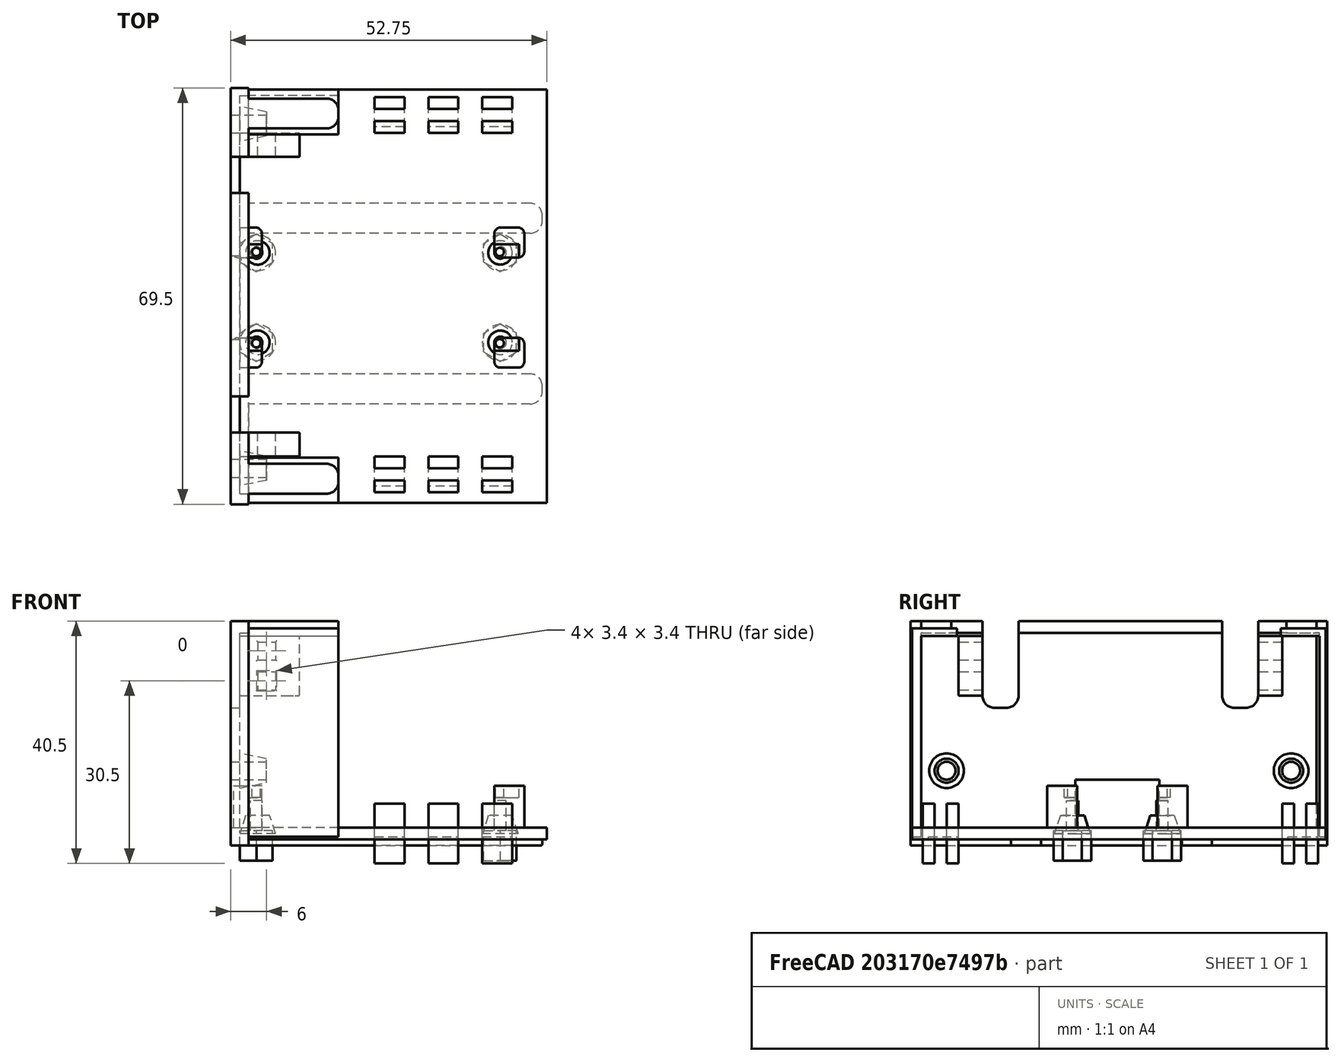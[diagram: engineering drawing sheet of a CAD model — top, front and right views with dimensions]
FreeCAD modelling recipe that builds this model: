
FCSTD DOCUMENT  (FreeCAD 0.19R24291 (Git))
Label: Arduino_Nano_33_BLE_tray_alt
License: All rights reserved
LicenseURL: http://en.wikipedia.org/wiki/All_rights_reserved
objects: Part::Box×67, Part::MultiFuse×33, Part::Fillet×18, Part::Cut×12, Part::Cylinder×10, Part::Cone×6, Part::MultiCommon×4
note: 150 computed .brp shape members not serialized (recipe doc carries the construction recipe); baked Part::Feature solids carry a one-line shape summary decoded from their .brp

FEATURE [Part::Box] Box  label="Board"
  AttacherType = Attacher::AttachEngine3D
  Height = 10
  Length = 45.16
  Width = 17.76
FEATURE [Part::Cylinder] Cylinder
  Angle = 360
  AttacherType = Attacher::AttachEngine3D
  Height = 10
  Placement = pos=(1.26,1.26,0) rot=(0,0,1;0rad)
  Radius = 0.7
FEATURE [Part::Cylinder] Cylinder001
  Angle = 360
  AttacherType = Attacher::AttachEngine3D
  Height = 10
  Placement = pos=(41.9,1.26,0) rot=(0,0,1;0rad)
  Radius = 0.7
FEATURE [Part::Cylinder] Cylinder002
  Angle = 360
  AttacherType = Attacher::AttachEngine3D
  Height = 10
  Placement = pos=(1.26,16.5,0) rot=(0,0,1;0rad)
  Radius = 0.7
FEATURE [Part::Cylinder] Cylinder003
  Angle = 360
  AttacherType = Attacher::AttachEngine3D
  Height = 10
  Placement = pos=(41.9,16.5,0) rot=(0,0,1;0rad)
  Radius = 0.7
FEATURE [Part::MultiFuse] Fusion  label="Holes"
  Shapes = -> [Cylinder,Cylinder001,Cylinder002,Cylinder003]
FEATURE [Part::Cut] Cut  label="Arduino_board_shape"
  Base = -> Box
  Placement = pos=(0,25.62,3) rot=(0,0,1;0rad)
  Tool = -> Fusion
FEATURE [Part::Box] Box001  label="Cube"
  AttacherType = Attacher::AttachEngine3D
  Height = 37.5
  Length = 3
  Placement = pos=(-3,0,0) rot=(0,0,1;0rad)
  Width = 69.5
FEATURE [Part::Box] Box002  label="Cube001"
  AttacherType = Attacher::AttachEngine3D
  Height = 2
  Length = 50
  Placement = pos=(-0.25,0.25,1) rot=(0,0,1;0rad)
  Width = 69
FEATURE [Part::Box] Box003  label="Cube002"
  AttacherType = Attacher::AttachEngine3D
  Height = 34.75
  Length = 15
  Placement = pos=(0,0,2) rot=(0,0,1;0rad)
  Width = 7.5
FEATURE [Part::Box] Box004  label="Cube003"
  AttacherType = Attacher::AttachEngine3D
  Height = 34.75
  Length = 15
  Placement = pos=(0,61.5,2) rot=(0,0,1;0rad)
  Width = 7.5
FEATURE [Part::Box] Box005  label="Cube004"
  AttacherType = Attacher::AttachEngine3D
  Height = 34
  Length = 15
  Placement = pos=(0,1.5,1) rot=(0,0,1;0rad)
  Width = 7.5
FEATURE [Part::Box] Box006  label="Cube005"
  AttacherType = Attacher::AttachEngine3D
  Height = 34
  Length = 15
  Placement = pos=(0,60,1) rot=(0,0,1;0rad)
  Width = 7.5
FEATURE [Part::MultiFuse] Fusion001
  Shapes = -> [Box006,Box005]
FEATURE [Part::MultiFuse] Fusion002
  Placement = pos=(0,0,-0.5) rot=(0,0,1;0rad)
  Shapes = -> [Box004,Box003]
FEATURE [Part::Cut] Cut001
  Base = -> Fusion002
  Placement = pos=(0,0.25,0) rot=(0,0,1;0rad)
  Tool = -> Fusion001
FEATURE [Part::Box] Box007  label="Cube006"
  AttacherType = Attacher::AttachEngine3D
  Height = 32.5
  Length = 3.5
  Placement = pos=(-1.5,1.75,3) rot=(0,0,1;0rad)
  Width = 66.5
FEATURE [Part::Cut] Cut002
  Base = -> Box001
  Tool = -> Box007
FEATURE [Part::Cylinder] Cylinder004
  Angle = 360
  AttacherType = Attacher::AttachEngine3D
  Height = 10
  Placement = pos=(-5,6,32.5) rot=(0,1,0;1.5708rad)
  Radius = 1.5
FEATURE [Part::Cylinder] Cylinder005
  Angle = 360
  AttacherType = Attacher::AttachEngine3D
  Height = 10
  Placement = pos=(-5,63.5,32.5) rot=(0,1,0;1.5708rad)
  Radius = 1.5
FEATURE [Part::MultiFuse] Fusion003
  Placement = pos=(0,0,-20) rot=(0,0,1;0rad)
  Shapes = -> [Cylinder004,Cylinder005]
FEATURE [Part::Box] Box008  label="Cube007"
  AttacherType = Attacher::AttachEngine3D
  Height = 8
  Length = 10
  Placement = pos=(-5,27.5,3) rot=(0,0,1;0rad)
  Width = 14
FEATURE [Part::Cone] Cone
  Angle = 360
  AttacherType = Attacher::AttachEngine3D
  Height = 5
  Placement = pos=(-1,6,32.5) rot=(0,1,0;1.5708rad)
  Radius1 = 3
  Radius2 = 2
FEATURE [Part::Cone] Cone001
  Angle = 360
  AttacherType = Attacher::AttachEngine3D
  Height = 5
  Placement = pos=(-1,63.5,32.5) rot=(0,1,0;1.5708rad)
  Radius1 = 3
  Radius2 = 2
FEATURE [Part::MultiFuse] Fusion004
  Placement = pos=(-1,0,-20) rot=(0,0,1;0rad)
  Shapes = -> [Cone,Cone001]
  expr: .Placement.Base.z = -20
FEATURE [Part::MultiFuse] Fusion005
  Shapes = -> [Cut002,Fusion004]
FEATURE [Part::Cut] Cut003
  Base = -> Fusion005
  Tool = -> Fusion003
FEATURE [Part::Cut] Cut004
  Base = -> Cut003
  Tool = -> Box008
FEATURE [Part::Cone] Cone002
  Angle = 360
  AttacherType = Attacher::AttachEngine3D
  Height = 3
  Placement = pos=(42,27,2) rot=(0,0,1;0rad)
  Radius1 = 3
  Radius2 = 2
FEATURE [Part::Box] Box014  label="Cube014"
  AttacherType = Attacher::AttachEngine3D
  Height = 5
  Length = 5.45
  Placement = pos=(3.25,0,0) rot=(0,0,1;0rad)
  Width = 10
FEATURE [Part::Box] Box015  label="Cube015"
  AttacherType = Attacher::AttachEngine3D
  Height = 5
  Length = 5.45
  Placement = pos=(11.5,4,0) rot=(0,0,1;2.0944rad)
  Width = 10
FEATURE [Part::Box] Box016  label="Cube016"
  AttacherType = Attacher::AttachEngine3D
  Height = 5
  Length = 10
  Placement = pos=(0.55,4,0) rot=(0,0,-1;0.523599rad)
  Width = 5.45
FEATURE [Part::Cylinder] Cylinder006
  Angle = 360
  AttacherType = Attacher::AttachEngine3D
  Height = 10
  Placement = pos=(4,4,-1) rot=(0,0,1;0rad)
  Radius = 1
FEATURE [Part::MultiCommon] Common  label="M.25 nut"
  Placement = pos=(-2,0,-1) rot=(0,0,1;0rad)
  Shapes = -> [Box014,Box016,Box015]
FEATURE [Part::MultiFuse] Fusion008  label="screw_hole"
  Placement = pos=(-2.7,23,0) rot=(0,0,1;0rad)
  Shapes = -> [Cylinder006,Common]
FEATURE [Part::Cone] Cone003
  Angle = 360
  AttacherType = Attacher::AttachEngine3D
  Height = 3
  Placement = pos=(42,42,2) rot=(0,0,1;0rad)
  Radius1 = 3
  Radius2 = 2
FEATURE [Part::Cone] Cone004
  Angle = 360
  AttacherType = Attacher::AttachEngine3D
  Height = 3
  Placement = pos=(1.5,42,2) rot=(0,0,1;0rad)
  Radius1 = 3
  Radius2 = 2
FEATURE [Part::Cone] Cone005
  Angle = 360
  AttacherType = Attacher::AttachEngine3D
  Height = 3
  Placement = pos=(1.5,27,2) rot=(0,0,1;0rad)
  Radius1 = 3
  Radius2 = 2
FEATURE [Part::Box] Box017  label="Cube017"
  AttacherType = Attacher::AttachEngine3D
  Height = 5
  Length = 5.45
  Placement = pos=(3.25,0,0) rot=(0,0,1;0rad)
  Width = 10
FEATURE [Part::Box] Box018  label="Cube018"
  AttacherType = Attacher::AttachEngine3D
  Height = 5
  Length = 5.45
  Placement = pos=(11.5,4,0) rot=(0,0,1;2.0944rad)
  Width = 10
FEATURE [Part::Cylinder] Cylinder007
  Angle = 360
  AttacherType = Attacher::AttachEngine3D
  Height = 10
  Placement = pos=(4,4,-1) rot=(0,0,1;0rad)
  Radius = 1
FEATURE [Part::Box] Box019  label="Cube019"
  AttacherType = Attacher::AttachEngine3D
  Height = 5
  Length = 10
  Placement = pos=(0.55,4,0) rot=(0,0,-1;0.523599rad)
  Width = 5.45
FEATURE [Part::MultiCommon] Common001  label="M.25 nut001"
  Placement = pos=(-2,0,-1) rot=(0,0,1;0rad)
  Shapes = -> [Box017,Box019,Box018]
FEATURE [Part::MultiFuse] Fusion009  label="screw_hole001"
  Placement = pos=(-2.7,38,0) rot=(0,0,1;0rad)
  Shapes = -> [Cylinder007,Common001]
FEATURE [Part::Box] Box020  label="Cube020"
  AttacherType = Attacher::AttachEngine3D
  Height = 5
  Length = 5.45
  Placement = pos=(3.25,0,0) rot=(0,0,1;0rad)
  Width = 10
FEATURE [Part::Box] Box021  label="Cube021"
  AttacherType = Attacher::AttachEngine3D
  Height = 5
  Length = 5.45
  Placement = pos=(11.5,4,0) rot=(0,0,1;2.0944rad)
  Width = 10
FEATURE [Part::Cylinder] Cylinder008
  Angle = 360
  AttacherType = Attacher::AttachEngine3D
  Height = 10
  Placement = pos=(4,4,-1) rot=(0,0,1;0rad)
  Radius = 1
FEATURE [Part::Box] Box022  label="Cube022"
  AttacherType = Attacher::AttachEngine3D
  Height = 5
  Length = 10
  Placement = pos=(0.55,4,0) rot=(0,0,-1;0.523599rad)
  Width = 5.45
FEATURE [Part::MultiCommon] Common002  label="M.25 nut002"
  Placement = pos=(-2,0,-1) rot=(0,0,1;0rad)
  Shapes = -> [Box020,Box022,Box021]
FEATURE [Part::MultiFuse] Fusion010  label="screw_hole002"
  Placement = pos=(38,23,0) rot=(0,0,1;0rad)
  Shapes = -> [Cylinder008,Common002]
FEATURE [Part::Box] Box023  label="Cube023"
  AttacherType = Attacher::AttachEngine3D
  Height = 5
  Length = 5.45
  Placement = pos=(3.25,0,0) rot=(0,0,1;0rad)
  Width = 10
FEATURE [Part::Box] Box024  label="Cube024"
  AttacherType = Attacher::AttachEngine3D
  Height = 5
  Length = 5.45
  Placement = pos=(11.5,4,0) rot=(0,0,1;2.0944rad)
  Width = 10
FEATURE [Part::Cylinder] Cylinder009
  Angle = 360
  AttacherType = Attacher::AttachEngine3D
  Height = 10
  Placement = pos=(4,4,-1) rot=(0,0,1;0rad)
  Radius = 1
FEATURE [Part::Box] Box025  label="Cube025"
  AttacherType = Attacher::AttachEngine3D
  Height = 5
  Length = 10
  Placement = pos=(0.55,4,0) rot=(0,0,-1;0.523599rad)
  Width = 5.45
FEATURE [Part::MultiCommon] Common003  label="M.25 nut003"
  Placement = pos=(-2,0,-1) rot=(0,0,1;0rad)
  Shapes = -> [Box023,Box025,Box024]
FEATURE [Part::MultiFuse] Fusion011  label="screw_hole003"
  Placement = pos=(38,38,0) rot=(0,0,1;0rad)
  Shapes = -> [Cylinder009,Common003]
FEATURE [Part::MultiFuse] Fusion012  label="Screw holes cut"
  Placement = pos=(0,0,-1.5) rot=(0,0,1;0rad)
  Shapes = -> [Fusion008,Fusion009,Fusion010,Fusion011]
FEATURE [Part::MultiFuse] Fusion014
  Shapes = -> [Cut004,Box002]
FEATURE [Part::MultiFuse] Fusion015
  Shapes = -> [Cut001]
FEATURE [Part::Box] Box026  label="Cube026"
  AttacherType = Attacher::AttachEngine3D
  Height = 15
  Length = 10
  Placement = pos=(0,0,16) rot=(0,0,1;0rad)
  Width = 6
FEATURE [Part::Fillet] Fillet012
  Base = -> Box026
  Edges = 2 edges r=2: [Edge9,Edge11]
  Placement = pos=(-4,12,7) rot=(0,0,1;0rad)
FEATURE [Part::Box] Box027  label="Cube027"
  AttacherType = Attacher::AttachEngine3D
  Height = 15
  Length = 10
  Placement = pos=(0,0,16) rot=(0,0,1;0rad)
  Width = 6
FEATURE [Part::Fillet] Fillet013
  Base = -> Box027
  Edges = 2 edges r=2: [Edge9,Edge11]
  Placement = pos=(-4,52,7) rot=(0,0,1;0rad)
FEATURE [Part::MultiFuse] Fusion016  label="Cables sockets"
  Shapes = -> [Fillet012,Fillet013]
FEATURE [Part::Cut] Cut006  label="Arduino_Nano_33_BLE_tray"
  Base = -> Fusion015
  Tool = -> Fusion016
FEATURE [Part::Box] Box028  label="Cube028"
  AttacherType = Attacher::AttachEngine3D
  Height = 2
  Length = 15
  Placement = pos=(0,-15.5,0) rot=(0,0,1;0rad)
  Width = 5
FEATURE [Part::Fillet] Fillet
  Base = -> Box028
  Edges = 2 edges r=2: [Edge5,Edge7]
  Placement = pos=(0,17,0) rot=(0,0,1;0rad)
FEATURE [Part::Box] Box029  label="Cube029"
  AttacherType = Attacher::AttachEngine3D
  Height = 2
  Length = 49
  Width = 5
FEATURE [Part::Fillet] Fillet014
  Base = -> Box029
  Edges = 2 edges r=2: [Edge5,Edge7]
  Placement = pos=(0,45,0) rot=(0,0,1;0rad)
FEATURE [Part::Fillet] Fillet015
  Base = -> Fillet
  Edges = 2 edges r=0.25: [Edge14,Edge16]
  Placement = pos=(0,0.25,35.5) rot=(0,0,1;0rad)
FEATURE [Part::Fillet] Fillet016
  Base = -> Fillet014
  Edges = 2 edges r=0.25: [Edge14,Edge16]
  Placement = pos=(0,0.25,0) rot=(0,0,1;0rad)
FEATURE [Part::Box] Box030  label="Cube030"
  AttacherType = Attacher::AttachEngine3D
  Height = 2
  Length = 49
  Width = 5
FEATURE [Part::Fillet] Fillet017
  Base = -> Box030
  Edges = 2 edges r=2: [Edge5,Edge7]
  Placement = pos=(0,17,0) rot=(0,0,1;0rad)
FEATURE [Part::Fillet] Fillet018
  Base = -> Fillet017
  Edges = 2 edges r=0.25: [Edge14,Edge16]
  Placement = pos=(0,-0.25,0) rot=(0,0,1;0rad)
FEATURE [Part::Box] Box031  label="Cube031"
  AttacherType = Attacher::AttachEngine3D
  Height = 2
  Length = 15
  Placement = pos=(0,-15.25,0) rot=(0,0,1;0rad)
  Width = 5
FEATURE [Part::Fillet] Fillet019
  Base = -> Box031
  Edges = 2 edges r=2: [Edge5,Edge7]
  Placement = pos=(0,17,0) rot=(0,0,1;0rad)
FEATURE [Part::Fillet] Fillet020
  Base = -> Fillet019
  Edges = 2 edges r=0.25: [Edge14,Edge16]
  Placement = pos=(0,61,35.5) rot=(0,0,1;0rad)
FEATURE [Part::MultiFuse] Fusion017  label="rails"
  Shapes = -> [Fillet015,Fillet016,Fillet018,Fillet020]
FEATURE [Part::MultiFuse] Fusion018  label="Arduino tray rough"
  Shapes = -> [Cut006,Fusion017]
FEATURE [Part::Box] Box032  label="Cube032"
  AttacherType = Attacher::AttachEngine3D
  Height = 10
  Length = 10
  Placement = pos=(0,8,26) rot=(0,0,1;0rad)
  Width = 4
FEATURE [Part::Box] Box033  label="Cube033"
  AttacherType = Attacher::AttachEngine3D
  Height = 3
  Length = 3
  Placement = pos=(3,5,27) rot=(0,0,1;0rad)
  Width = 10
FEATURE [Part::Box] Box034  label="Cube034"
  AttacherType = Attacher::AttachEngine3D
  Height = 3
  Length = 3
  Placement = pos=(3,5,32) rot=(0,0,1;0rad)
  Width = 10
FEATURE [Part::MultiFuse] Fusion019
  Shapes = -> [Box033,Box034]
FEATURE [Part::Cut] Cut007
  Base = -> Box032
  Tool = -> Fusion019
FEATURE [Part::Fillet] Fillet022  label="zip ties holder"
  Base = -> Cut007
  Edges = 22 edges r=0.2: [Edge5,Edge6,Edge7,Edge8,Edge9,Edge10,Edge11,Edge12,Edge13,Edge14,Edge15,Edge16,Edge19,Edge20,Edge21,Edge22,Edge23,Edge24,Edge25,Edge26,Edge27,Edge28]
  Placement = pos=(-1,0,-1) rot=(0,0,1;0rad)
FEATURE [Part::Box] Box035  label="Cube035"
  AttacherType = Attacher::AttachEngine3D
  Height = 10
  Length = 10
  Placement = pos=(0,10,26) rot=(0,0,1;0rad)
  Width = 4
FEATURE [Part::Box] Box036  label="Cube036"
  AttacherType = Attacher::AttachEngine3D
  Height = 3
  Length = 3
  Placement = pos=(3,10,27) rot=(0,0,1;0rad)
  Width = 10
FEATURE [Part::Box] Box037  label="Cube037"
  AttacherType = Attacher::AttachEngine3D
  Height = 3
  Length = 3
  Placement = pos=(3,10,32) rot=(0,0,1;0rad)
  Width = 10
FEATURE [Part::MultiFuse] Fusion020
  Shapes = -> [Box036,Box037]
FEATURE [Part::Cut] Cut008
  Base = -> Box035
  Tool = -> Fusion020
FEATURE [Part::Fillet] Fillet023  label="zip ties holder001"
  Base = -> Cut008
  Edges = 22 edges r=0.2: [Edge5,Edge6,Edge7,Edge8,Edge9,Edge10,Edge11,Edge12,Edge13,Edge14,Edge15,Edge16,Edge19,Edge20,Edge21,Edge22,Edge23,Edge24,Edge25,Edge26,Edge27,Edge28]
  Placement = pos=(-1,48,-1) rot=(0,0,1;0rad)
FEATURE [Part::MultiFuse] Fusion021  label="zip ties holders"
  Placement = pos=(-0.5,0,0) rot=(0,0,1;0rad)
  Shapes = -> [Fillet022,Fillet023]
FEATURE [Part::Box] Box038  label="Cube038"
  AttacherType = Attacher::AttachEngine3D
  Height = 10
  Length = 5
  Placement = pos=(21,2,-3) rot=(0,0,1;0rad)
  Width = 2
FEATURE [Part::Box] Box039  label="Cube039"
  AttacherType = Attacher::AttachEngine3D
  Height = 10
  Length = 5
  Placement = pos=(30,2,-3) rot=(0,0,1;0rad)
  Width = 2
FEATURE [Part::Box] Box040  label="Cube040"
  AttacherType = Attacher::AttachEngine3D
  Height = 10
  Length = 5
  Placement = pos=(39,2,-3) rot=(0,0,1;0rad)
  Width = 2
FEATURE [Part::MultiFuse] Fusion022  label="zip ties holes board r"
  Shapes = -> [Box038,Box039,Box040]
FEATURE [Part::Box] Box041  label="Cube041"
  AttacherType = Attacher::AttachEngine3D
  Height = 10
  Length = 5
  Placement = pos=(21,2,-3) rot=(0,0,1;0rad)
  Width = 2
FEATURE [Part::Box] Box042  label="Cube042"
  AttacherType = Attacher::AttachEngine3D
  Height = 10
  Length = 5
  Placement = pos=(30,2,-3) rot=(0,0,1;0rad)
  Width = 2
FEATURE [Part::Box] Box043  label="Cube043"
  AttacherType = Attacher::AttachEngine3D
  Height = 10
  Length = 5
  Placement = pos=(39,2,-3) rot=(0,0,1;0rad)
  Width = 2
FEATURE [Part::MultiFuse] Fusion023  label="zip ties holes board l"
  Placement = pos=(0,64,0) rot=(0,0,1;0rad)
  Shapes = -> [Box041,Box042,Box043]
FEATURE [Part::Box] Box044  label="Cube044"
  AttacherType = Attacher::AttachEngine3D
  Height = 10
  Length = 5
  Placement = pos=(21,2,-3) rot=(0,0,1;0rad)
  Width = 2
FEATURE [Part::Box] Box045  label="Cube045"
  AttacherType = Attacher::AttachEngine3D
  Height = 10
  Length = 5
  Placement = pos=(30,2,-3) rot=(0,0,1;0rad)
  Width = 2
FEATURE [Part::Box] Box046  label="Cube046"
  AttacherType = Attacher::AttachEngine3D
  Height = 10
  Length = 5
  Placement = pos=(39,2,-3) rot=(0,0,1;0rad)
  Width = 2
FEATURE [Part::MultiFuse] Fusion024  label="zip ties holes board r001"
  Placement = pos=(0,4,0) rot=(0,0,1;0rad)
  Shapes = -> [Box044,Box045,Box046]
FEATURE [Part::Box] Box047  label="Cube047"
  AttacherType = Attacher::AttachEngine3D
  Height = 10
  Length = 5
  Placement = pos=(21,2,-3) rot=(0,0,1;0rad)
  Width = 2
FEATURE [Part::Box] Box048  label="Cube048"
  AttacherType = Attacher::AttachEngine3D
  Height = 10
  Length = 5
  Placement = pos=(30,2,-3) rot=(0,0,1;0rad)
  Width = 2
FEATURE [Part::Box] Box049  label="Cube049"
  AttacherType = Attacher::AttachEngine3D
  Height = 10
  Length = 5
  Placement = pos=(39,2,-3) rot=(0,0,1;0rad)
  Width = 2
FEATURE [Part::MultiFuse] Fusion025  label="zip ties holes board l001"
  Placement = pos=(0,60,0) rot=(0,0,1;0rad)
  Shapes = -> [Box047,Box048,Box049]
FEATURE [Part::MultiFuse] Fusion026  label="zip ties holes"
  Shapes = -> [Fusion022,Fusion023,Fusion024,Fusion025]
FEATURE [Part::MultiFuse] Fusion027  label="Arduino_tray"
  Shapes = -> [Fusion021]
FEATURE [Part::Box] Box050  label="Cube050"
  AttacherType = Attacher::AttachEngine3D
  Height = 1.5
  Length = 5
  Placement = pos=(21,3,0) rot=(0,0,1;0rad)
  Width = 5
FEATURE [Part::Box] Box051  label="Cube051"
  AttacherType = Attacher::AttachEngine3D
  Height = 1.5
  Length = 5
  Placement = pos=(30,3,0) rot=(0,0,1;0rad)
  Width = 5
FEATURE [Part::Box] Box052  label="Cube052"
  AttacherType = Attacher::AttachEngine3D
  Height = 1.5
  Length = 5
  Placement = pos=(39,3,0) rot=(0,0,1;0rad)
  Width = 5
FEATURE [Part::Box] Box053  label="Cube053"
  AttacherType = Attacher::AttachEngine3D
  Height = 1.5
  Length = 5
  Placement = pos=(39,63,0) rot=(0,0,1;0rad)
  Width = 5
FEATURE [Part::Box] Box054  label="Cube054"
  AttacherType = Attacher::AttachEngine3D
  Height = 1.5
  Length = 5
  Placement = pos=(30,63,0) rot=(0,0,1;0rad)
  Width = 5
FEATURE [Part::Box] Box055  label="Cube055"
  AttacherType = Attacher::AttachEngine3D
  Height = 1.5
  Length = 5
  Placement = pos=(21,63,0) rot=(0,0,1;0rad)
  Width = 5
FEATURE [Part::MultiFuse] Fusion028
  Shapes = -> [Box050,Box051,Box052,Box053,Box054,Box055]
FEATURE [Part::Cut] Cut010
  Base = -> Fusion027
  Tool = -> Fusion028
FEATURE [Part::Box] Box056  label="Cube056"
  AttacherType = Attacher::AttachEngine3D
  Height = 7
  Length = 5
  Placement = pos=(-2.8,22.8,-2) rot=(0,0,1;0rad)
  Width = 5
FEATURE [Part::Box] Box057  label="Cube057"
  AttacherType = Attacher::AttachEngine3D
  Height = 7
  Length = 5
  Placement = pos=(-2.8,41.2,-2) rot=(0,0,1;0rad)
  Width = 5
FEATURE [Part::Box] Box058  label="Cube058"
  AttacherType = Attacher::AttachEngine3D
  Height = 7
  Length = 5
  Placement = pos=(41,41.2,-2) rot=(0,0,1;0rad)
  Width = 5
FEATURE [Part::Box] Box059  label="Cube059"
  AttacherType = Attacher::AttachEngine3D
  Height = 7
  Length = 5
  Placement = pos=(41,22.8,-2) rot=(0,0,1;0rad)
  Width = 5
FEATURE [Part::Fillet] Fillet024
  Base = -> Box056
  Edges = 4 edges r=1: [Edge1,Edge3,Edge5,Edge7]
FEATURE [Part::Fillet] Fillet025
  Base = -> Box057
  Edges = 4 edges r=1: [Edge1,Edge3,Edge5,Edge7]
FEATURE [Part::Fillet] Fillet026
  Base = -> Box058
  Edges = 4 edges r=1: [Edge1,Edge3,Edge5,Edge7]
FEATURE [Part::Fillet] Fillet027
  Base = -> Box059
  Edges = 4 edges r=1: [Edge1,Edge3,Edge5,Edge7]
FEATURE [Part::MultiFuse] Fusion029
  Shapes = -> [Fillet024,Fillet025,Fillet026,Fillet027]
FEATURE [Part::Cut] Cut011
  Base = -> Fusion029
  Placement = pos=(0,0,5) rot=(0,0,1;0rad)
  Tool = -> Cut
FEATURE [Part::Box] Box060  label="Cube060"
  AttacherType = Attacher::AttachEngine3D
  Height = 34.75
  Length = 15
  Placement = pos=(0,0,2) rot=(0,0,1;0rad)
  Width = 7.5
FEATURE [Part::Box] Box061  label="Cube061"
  AttacherType = Attacher::AttachEngine3D
  Height = 34.75
  Length = 15
  Placement = pos=(0,61.5,2) rot=(0,0,1;0rad)
  Width = 7.5
FEATURE [Part::Box] Box062  label="Cube062"
  AttacherType = Attacher::AttachEngine3D
  Height = 34
  Length = 15
  Placement = pos=(0,1.5,1) rot=(0,0,1;0rad)
  Width = 7.5
FEATURE [Part::Box] Box063  label="Cube063"
  AttacherType = Attacher::AttachEngine3D
  Height = 34
  Length = 15
  Placement = pos=(0,60.5,1) rot=(0,0,1;0rad)
  Width = 7.5
FEATURE [Part::MultiFuse] Fusion030
  Shapes = -> [Box063,Box062]
FEATURE [Part::MultiFuse] Fusion031
  Placement = pos=(0,0,-0.5) rot=(0,0,1;0rad)
  Shapes = -> [Box061,Box060]
FEATURE [Part::Cut] Cut012
  Base = -> Fusion031
  Placement = pos=(0,0.25,0) rot=(0,0,1;0rad)
  Tool = -> Fusion030
FEATURE [Part::Box] Box064  label="Cube064"
  AttacherType = Attacher::AttachEngine3D
  Height = 15
  Length = 10
  Placement = pos=(0,0,16) rot=(0,0,1;0rad)
  Width = 6
FEATURE [Part::Fillet] Fillet028
  Base = -> Box064
  Edges = 2 edges r=2: [Edge9,Edge11]
  Placement = pos=(-4,12,7) rot=(0,0,1;0rad)
FEATURE [Part::Box] Box065  label="Cube065"
  AttacherType = Attacher::AttachEngine3D
  Height = 15
  Length = 10
  Placement = pos=(0,0,16) rot=(0,0,1;0rad)
  Width = 6
FEATURE [Part::Fillet] Fillet029
  Base = -> Box065
  Edges = 2 edges r=2: [Edge9,Edge11]
  Placement = pos=(-4,52,7) rot=(0,0,1;0rad)
FEATURE [Part::MultiFuse] Fusion032  label="Cables sockets001"
  Shapes = -> [Fillet028,Fillet029]
FEATURE [Part::MultiFuse] Fusion033
  Shapes = -> [Fusion014,Fusion018,Cut010,Cut011]
FEATURE [Part::Box] Box066  label="Cube066"
  AttacherType = Attacher::AttachEngine3D
  Height = 1.5
  Length = 5
  Placement = pos=(21,3,0) rot=(0,0,1;0rad)
  Width = 5
FEATURE [Part::Box] Box067  label="Cube067"
  AttacherType = Attacher::AttachEngine3D
  Height = 1.5
  Length = 5
  Placement = pos=(30,3,0) rot=(0,0,1;0rad)
  Width = 5
FEATURE [Part::Box] Box068  label="Cube068"
  AttacherType = Attacher::AttachEngine3D
  Height = 1.5
  Length = 5
  Placement = pos=(39,3,0) rot=(0,0,1;0rad)
  Width = 5
FEATURE [Part::Box] Box069  label="Cube069"
  AttacherType = Attacher::AttachEngine3D
  Height = 1.5
  Length = 5
  Placement = pos=(39,63,0) rot=(0,0,1;0rad)
  Width = 5
FEATURE [Part::Box] Box070  label="Cube070"
  AttacherType = Attacher::AttachEngine3D
  Height = 1.5
  Length = 5
  Placement = pos=(30,63,0) rot=(0,0,1;0rad)
  Width = 5
FEATURE [Part::Box] Box071  label="Cube071"
  AttacherType = Attacher::AttachEngine3D
  Height = 1.5
  Length = 5
  Placement = pos=(21,63,0) rot=(0,0,1;0rad)
  Width = 5
FEATURE [Part::MultiFuse] Fusion034
  Shapes = -> [Box066,Box067,Box068,Box069,Box070,Box071]
FEATURE [Part::MultiFuse] Fusion035
  Shapes = -> [Fusion034,Fusion032]
FEATURE [Part::Cut] Cut013
  Base = -> Fusion033
  Tool = -> Fusion035
